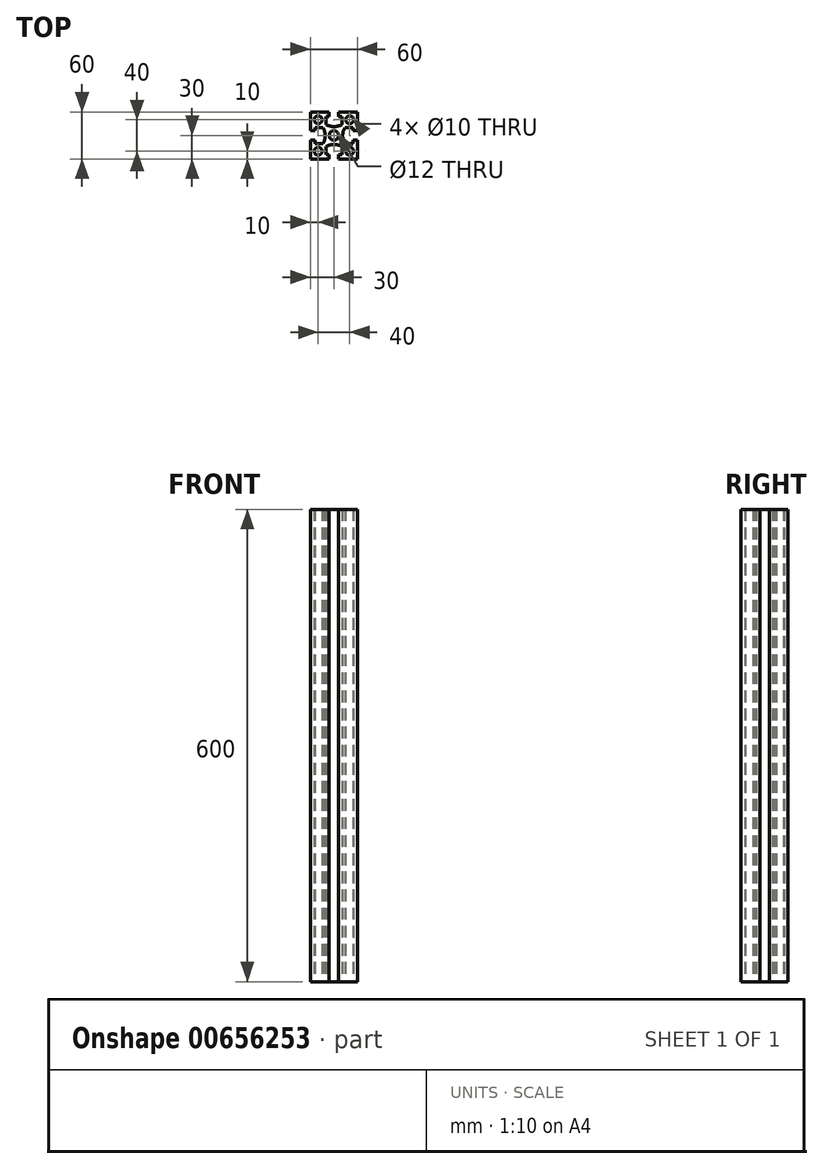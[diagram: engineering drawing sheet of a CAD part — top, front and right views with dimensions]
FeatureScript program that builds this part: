
annotation { "Feature Type Name" : "Feature", "Feature Type Description" : "" }
export const myFeature = defineFeature(function(context is Context, id is Id, definition is map)
    precondition{}
    {
        {
            var Q0;
            Q0=qCreatedBy(makeId("Top.planeOp"),FACE);
            var sketch = newSketch(context, id + "F0", { "sketchPlane" : qUnion([Q0])});
            skLineSegment(sketch, "E0.bottom", {"start": v(30, 30) * mm, "end": v(6, 30) * mm});
            skLineSegment(sketch, "E0.top", {"start": v(30, -30) * mm, "end": v(6, -30) * mm});
            skLineSegment(sketch, "E0.left", {"start": v(30, 30) * mm, "end": v(30, 6) * mm});
            skLineSegment(sketch, "E0.right", {"start": v(-30, 30) * mm, "end": v(-30, 6) * mm});
            skPoint(sketch, "E0.middle", {"position": v(0, 0) * mm});
            skCircle(sketch, "E1", {"center": v(20, -20) * mm, "radius": 5 * mm});
            skCircle(sketch, "E2", {"center": v(20, 20) * mm, "radius": 5 * mm});
            skLineSegment(sketch, "E3", {"start": v(0, -30) * mm, "end": v(0, 30) * mm});
            skLineSegment(sketch, "E4", {"start": v(6, 30) * mm, "end": v(6, 24) * mm});
            skLineSegment(sketch, "E5", {"start": v(6, 24) * mm, "end": v(10, 24) * mm});
            skLineSegment(sketch, "E6", {"start": v(10, 24) * mm, "end": v(10, 14) * mm});
            skCircle(sketch, "E7", {"center": v(0, 0) * mm, "radius": 6 * mm});
            skLineSegment(sketch, "E8.MirrorCS", {"start": v(-6, 30) * mm, "end": v(-6, 24) * mm});
            skLineSegment(sketch, "E9.MirrorCS", {"start": v(-6, 24) * mm, "end": v(-10, 24) * mm});
            skLineSegment(sketch, "E10.MirrorCS", {"start": v(-10, 24) * mm, "end": v(-10, 14) * mm});
            skLineSegment(sketch, "E11.MirrorCS", {"start": v(-10, -24) * mm, "end": v(-10, -14) * mm});
            skArc(sketch, "E12.MirrorCS", {"start": v(-10, -14) * mm, "mid": v(0, -11.32) * mm, "end": v(10, -14) * mm});
            skLineSegment(sketch, "E13.MirrorCS", {"start": v(10, -24) * mm, "end": v(10, -14) * mm});
            skLineSegment(sketch, "E14.MirrorCS", {"start": v(6, -24) * mm, "end": v(10, -24) * mm});
            skLineSegment(sketch, "E15.MirrorCS", {"start": v(6, -30) * mm, "end": v(6, -24) * mm});
            skLineSegment(sketch, "E16.MirrorCS", {"start": v(-6, -30) * mm, "end": v(-6, -24) * mm});
            skLineSegment(sketch, "E17.MirrorCS", {"start": v(-6, -24) * mm, "end": v(-10, -24) * mm});
            skLineSegment(sketch, "E18.2.1", {"start": v(-30, 6) * mm, "end": v(-24, 6) * mm});
            skLineSegment(sketch, "E18.2.2", {"start": v(-24, 6) * mm, "end": v(-24, 10) * mm});
            skLineSegment(sketch, "E18.2.3", {"start": v(-24, 10) * mm, "end": v(-14, 10) * mm});
            skArc(sketch, "E18.2.4", {"start": v(-14, -10) * mm, "mid": v(-11.13, 0) * mm, "end": v(-14, 10) * mm});
            skLineSegment(sketch, "E18.2.5", {"start": v(-24, -10) * mm, "end": v(-14, -10) * mm});
            skLineSegment(sketch, "E18.2.6", {"start": v(-30, -6) * mm, "end": v(-24, -6) * mm});
            skLineSegment(sketch, "E18.2.7", {"start": v(-24, -6) * mm, "end": v(-24, -10) * mm});
            skLineSegment(sketch, "E19.MirrorCS", {"start": v(24, 10) * mm, "end": v(14, 10) * mm});
            skLineSegment(sketch, "E20.MirrorCS", {"start": v(30, 6) * mm, "end": v(24, 6) * mm});
            skLineSegment(sketch, "E21.MirrorCS", {"start": v(24, 6) * mm, "end": v(24, 10) * mm});
            skArc(sketch, "E22.MirrorCS", {"start": v(14, -10) * mm, "mid": v(11.13, 0) * mm, "end": v(14, 10) * mm});
            skLineSegment(sketch, "E23.MirrorCS", {"start": v(24, -10) * mm, "end": v(14, -10) * mm});
            skLineSegment(sketch, "E24.MirrorCS", {"start": v(24, -6) * mm, "end": v(24, -10) * mm});
            skLineSegment(sketch, "E25.MirrorCS", {"start": v(30, -6) * mm, "end": v(24, -6) * mm});
            skCircle(sketch, "E26.MirrorC", {"center": v(-20, -20) * mm, "radius": 5 * mm});
            skCircle(sketch, "E27.MirrorC", {"center": v(-20, 20) * mm, "radius": 5 * mm});
            skLineSegment(sketch, "E28.trimOffspring", {"start": v(-6, 30) * mm, "end": v(-30, 30) * mm});
            skLineSegment(sketch, "E29.trimOffspring", {"start": v(30, -6) * mm, "end": v(30, -30) * mm});
            skLineSegment(sketch, "E30.trimOffspring", {"start": v(-30, -6) * mm, "end": v(-30, -30) * mm});
            skLineSegment(sketch, "E31.trimOffspring", {"start": v(-6, -30) * mm, "end": v(-30, -30) * mm});
            skArc(sketch, "E32", {"start": v(-10, 14) * mm, "mid": v(0, 11.32) * mm, "end": v(10, 14) * mm});
            skSolve(sketch);
        }
        {
            var Q0;
            Q0=makeQuery(id+"F0.imprint","IMPRINT",FACE,{"disambiguationData":[TD([[makeQuery(id+"F0.imprint","IMPRINT",EDGE,{"derivedFrom":sQuery(id+"F0.wireOp",EDGE,"E0.bottom")}),1.0]])]});
            var Q1;
            Q1=makeQuery(id+"F0.imprint","IMPRINT",FACE,{"disambiguationData":[TD([[makeQuery(id+"F0.imprint","IMPRINT",EDGE,{"derivedFrom":sQuery(id+"F0.wireOp",EDGE,"E0.right")}),1.0]])]});
            extrude(context, id + "F1", {"entities" : qUnion([Q0, Q1]), "depth" : 600 * mm, "offsetDistance" : 25 * mm});
        }
    });
